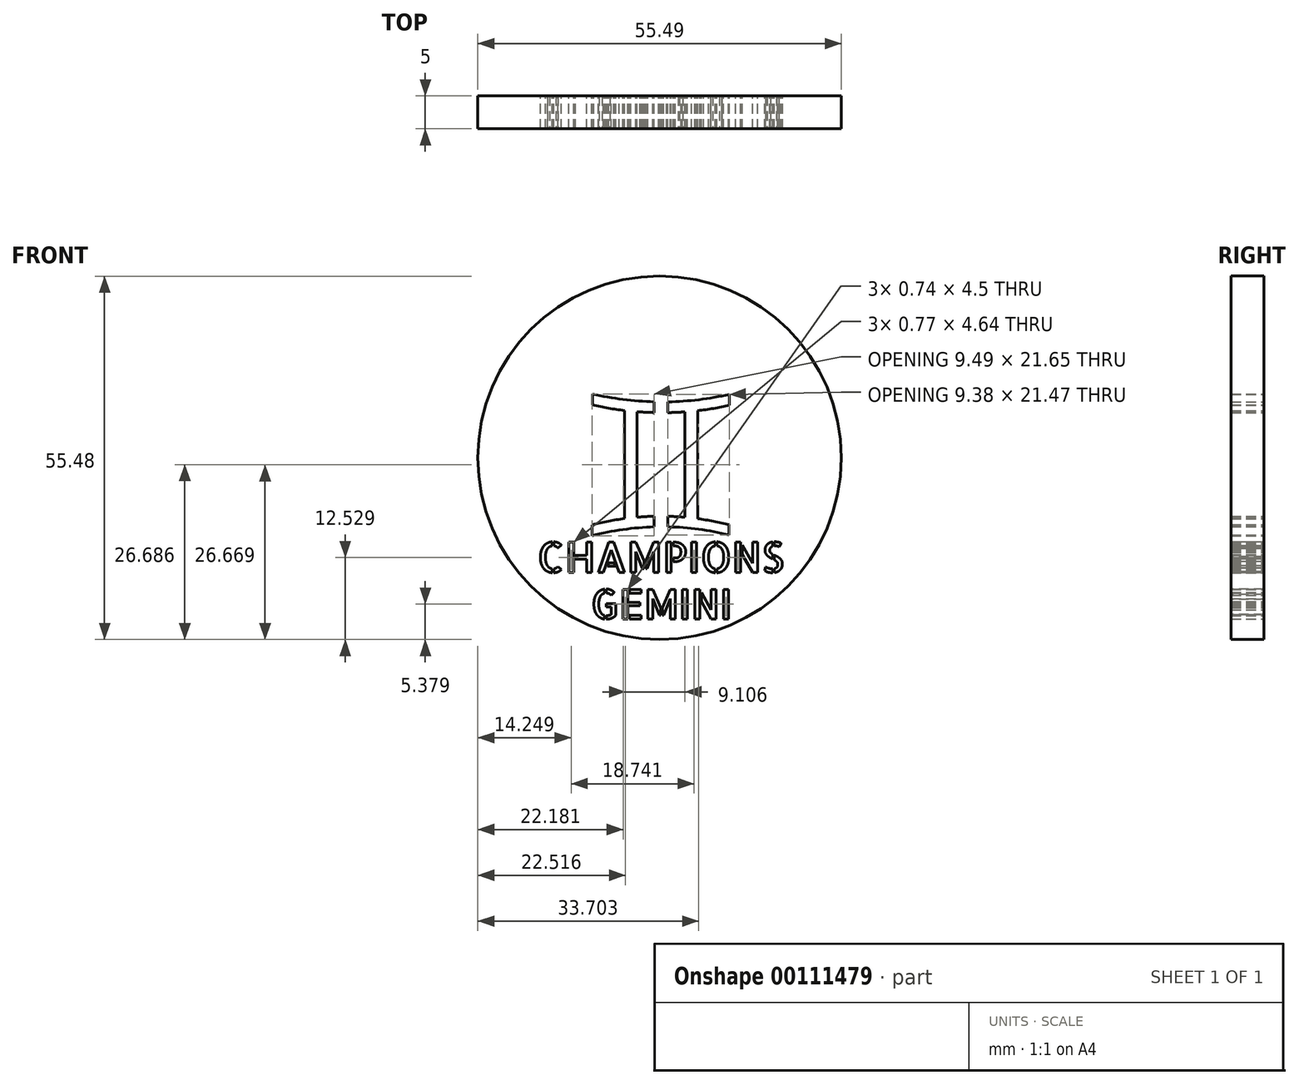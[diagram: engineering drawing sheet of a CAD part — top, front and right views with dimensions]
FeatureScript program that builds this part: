
annotation { "Feature Type Name" : "Feature", "Feature Type Description" : "" }
export const myFeature = defineFeature(function(context is Context, id is Id, definition is map)
    precondition{}
    {
        {
            var Q0;
            Q0=qCreatedBy(makeId("Front.planeOp"),FACE);
            var sketch = newSketch(context, id + "F0", { "sketchPlane" : qUnion([Q0])});
            skCircle(sketch, "E0", {"center": v(-0.65, -0.74) * mm, "radius": 27.74 * mm});
            skPoint(sketch, "E0.first.point", {"position": v(0, 27) * mm});
            skPoint(sketch, "E0.second.point", {"position": v(-1.07, -28.48) * mm});
            skPoint(sketch, "E0.third.point", {"position": v(-28.34, 0.92) * mm});
            skArc(sketch, "E1", {"start": v(-10.91, 9.01) * mm, "mid": v(-6.22, 8.17) * mm, "end": v(-1.46, 7.8) * mm});
            skArc(sketch, "E2.0", {"start": v(-10.91, 7.32) * mm, "mid": v(-6.22, 6.51) * mm, "end": v(-1.46, 6.16) * mm});
            skLineSegment(sketch, "E3", {"start": v(-10.91, 9.01) * mm, "end": v(-10.91, 7.32) * mm});
            skLineSegment(sketch, "E4", {"start": v(10, 8.94) * mm, "end": v(10, 7.25) * mm});
            skLineSegment(sketch, "E5", {"start": v(-6, 6.49) * mm, "end": v(-6, -9.99) * mm});
            skLineSegment(sketch, "E6", {"start": v(-4.06, 6.3) * mm, "end": v(-4.06, -9.88) * mm});
            skLineSegment(sketch, "E7", {"start": v(3.22, 6.28) * mm, "end": v(3.22, -9.9) * mm});
            skLineSegment(sketch, "E8", {"start": v(5.17, 6.46) * mm, "end": v(5.17, -10.04) * mm});
            skArc(sketch, "E9", {"start": v(9.95, -10.96) * mm, "mid": v(5.32, -10.06) * mm, "end": v(0.62, -9.67) * mm});
            skArc(sketch, "E10", {"start": v(9.95, -12.53) * mm, "mid": v(5.32, -11.64) * mm, "end": v(0.62, -11.28) * mm});
            skLineSegment(sketch, "E11", {"start": v(5.17, -10.04) * mm, "end": v(5.17, -10.1) * mm});
            skLineSegment(sketch, "E12", {"start": v(9.95, -10.96) * mm, "end": v(9.95, -12.53) * mm});
            skLineSegment(sketch, "E13", {"start": v(-10.96, -10.98) * mm, "end": v(-10.94, -12.64) * mm});
            skLineSegment(sketch, "E14", {"start": v(-6, -9.99) * mm, "end": v(-6, -10.31) * mm});
            skText(sketch, "E15", { "text": "CHAMPIONS", "fontName": "AllertaStencil-Regular.ttf"});
            skText(sketch, "E16", { "text": "GEMINI", "fontName": "AllertaStencil-Regular.ttf"});
            skLineSegment(sketch, "E17", {"start": v(0.62, 6.16) * mm, "end": v(0.62, 6.2) * mm});
            skLineSegment(sketch, "E18", {"start": v(-1.46, 6.2) * mm, "end": v(-1.46, 7.8) * mm});
            skLineSegment(sketch, "E19", {"start": v(0.62, 6.2) * mm, "end": v(0.62, 7.8) * mm});
            skArc(sketch, "E20.trimOffspring", {"start": v(0.62, 6.16) * mm, "mid": v(5.34, 6.48) * mm, "end": v(10, 7.25) * mm});
            skArc(sketch, "E21.trimOffspring", {"start": v(0.62, 7.8) * mm, "mid": v(5.34, 8.14) * mm, "end": v(10, 8.94) * mm});
            skArc(sketch, "E22.trimOffspring", {"start": v(-1.46, -9.67) * mm, "mid": v(-6.25, -10.05) * mm, "end": v(-10.96, -10.98) * mm});
            skArc(sketch, "E23.trimOffspring", {"start": v(-1.46, -11.29) * mm, "mid": v(-6.24, -11.7) * mm, "end": v(-10.94, -12.64) * mm});
            skLineSegment(sketch, "E24", {"start": v(-1.46, -9.67) * mm, "end": v(-1.46, -11.29) * mm});
            skLineSegment(sketch, "E25", {"start": v(0.62, -9.67) * mm, "end": v(0.62, -11.28) * mm});
            skLineSegment(sketch, "E26", {"start": v(-6, 6.49) * mm, "end": v(-6, 6.61) * mm});
            skLineSegment(sketch, "E27", {"start": v(-4.06, 6.3) * mm, "end": v(-4.06, 6.45) * mm});
            skLineSegment(sketch, "E28", {"start": v(3.22, 6.15) * mm, "end": v(3.22, 6.75) * mm});
            skLineSegment(sketch, "E29", {"start": v(5.17, 6.22) * mm, "end": v(5.17, 6.74) * mm});
            skLineSegment(sketch, "E30", {"start": v(-1.46, 6.2) * mm, "end": v(-1.46, 6.16) * mm});
            const initialGuessF0  = {"E15": [-0.01934, -0.01827, 1, 0, 0.00464], "E16": [-0.01116, -0.02535, 1, 0, 0.0045]};
            skSetInitialGuess(sketch, initialGuessF0);
            skSolve(sketch);
        }
        {
            var Q0;
            Q0=makeQuery(id+"F0.imprint","IMPRINT",FACE,{"disambiguationData":[TD([[makeQuery(id+"F0.imprint","IMPRINT",EDGE,{"derivedFrom":sQuery(id+"F0.wireOp",EDGE,"E0")}),1.0]])]});
            extrude(context, id + "F1", {"entities" : qUnion([Q0]), "depth" : 5 * mm});
        }
    });
